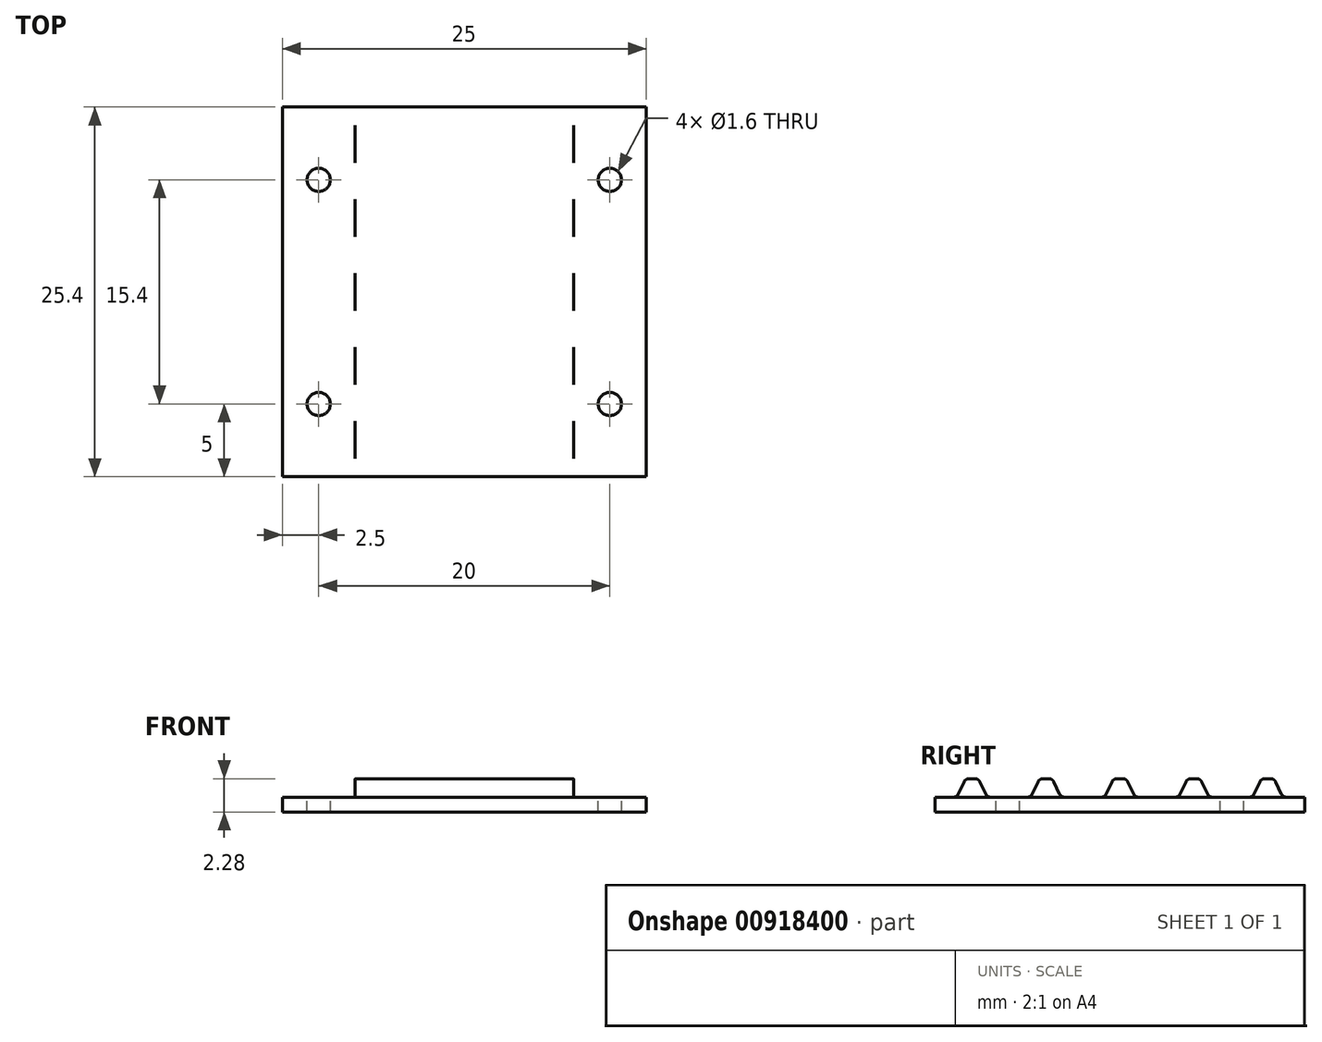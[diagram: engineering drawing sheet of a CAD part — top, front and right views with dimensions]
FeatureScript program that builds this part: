
annotation { "Feature Type Name" : "Feature", "Feature Type Description" : "" }
export const myFeature = defineFeature(function(context is Context, id is Id, definition is map)
    precondition{}
    {
        {
            var Q0;
            Q0=qCreatedBy(makeId("Right.planeOp"),FACE);
            var sketch = newSketch(context, id + "F0", { "sketchPlane" : qUnion([Q0])});
            skArc(sketch, "E0", {"start": v(8.88, -0.13) * mm, "mid": v(9.08, -0.07) * mm, "end": v(9.22, 0.1) * mm});
            skLineSegment(sketch, "E1", {"start": v(9.22, 0.1) * mm, "end": v(9.6, 0.92) * mm});
            skArc(sketch, "E2", {"start": v(9.95, 1.14) * mm, "mid": v(9.75, 1.08) * mm, "end": v(9.6, 0.92) * mm});
            skLineSegment(sketch, "E3", {"start": v(9.95, 1.14) * mm, "end": v(10.37, 1.14) * mm});
            skArc(sketch, "E4", {"start": v(10.7, 0.93) * mm, "mid": v(10.57, 1.08) * mm, "end": v(10.37, 1.14) * mm});
            skLineSegment(sketch, "E5", {"start": v(10.7, 0.93) * mm, "end": v(11.1, 0.1) * mm});
            skArc(sketch, "E6", {"start": v(11.1, 0.1) * mm, "mid": v(11.24, -0.07) * mm, "end": v(11.44, -0.13) * mm});
            skLineSegment(sketch, "E7", {"start": v(11.44, -0.13) * mm, "end": v(12.7, -0.13) * mm});
            skLineSegment(sketch, "E8", {"start": v(12.7, -0.13) * mm, "end": v(12.7, -1.14) * mm});
            skArc(sketch, "E9", {"start": v(3.8, -0.13) * mm, "mid": v(4, -0.07) * mm, "end": v(4.14, 0.1) * mm});
            skLineSegment(sketch, "E10", {"start": v(4.14, 0.1) * mm, "end": v(4.53, 0.92) * mm});
            skArc(sketch, "E11", {"start": v(4.87, 1.14) * mm, "mid": v(4.67, 1.08) * mm, "end": v(4.53, 0.92) * mm});
            skLineSegment(sketch, "E12", {"start": v(4.87, 1.14) * mm, "end": v(5.29, 1.14) * mm});
            skArc(sketch, "E13", {"start": v(5.63, 0.93) * mm, "mid": v(5.49, 1.08) * mm, "end": v(5.29, 1.14) * mm});
            skLineSegment(sketch, "E14", {"start": v(5.63, 0.93) * mm, "end": v(6.02, 0.1) * mm});
            skArc(sketch, "E15", {"start": v(6.02, 0.1) * mm, "mid": v(6.16, -0.07) * mm, "end": v(6.36, -0.13) * mm});
            skLineSegment(sketch, "E16", {"start": v(6.36, -0.13) * mm, "end": v(8.88, -0.13) * mm});
            skArc(sketch, "E17", {"start": v(-1.28, -0.13) * mm, "mid": v(-1.08, -0.07) * mm, "end": v(-0.94, 0.1) * mm});
            skLineSegment(sketch, "E18", {"start": v(-0.94, 0.1) * mm, "end": v(-0.55, 0.92) * mm});
            skArc(sketch, "E19", {"start": v(-0.2, 1.14) * mm, "mid": v(-0.41, 1.08) * mm, "end": v(-0.55, 0.92) * mm});
            skLineSegment(sketch, "E20", {"start": v(-0.2, 1.14) * mm, "end": v(0.2, 1.14) * mm});
            skArc(sketch, "E21", {"start": v(0.55, 0.93) * mm, "mid": v(0.4, 1.08) * mm, "end": v(0.2, 1.14) * mm});
            skLineSegment(sketch, "E22", {"start": v(0.55, 0.93) * mm, "end": v(0.94, 0.1) * mm});
            skArc(sketch, "E23", {"start": v(0.94, 0.1) * mm, "mid": v(1.08, -0.07) * mm, "end": v(1.28, -0.13) * mm});
            skLineSegment(sketch, "E24", {"start": v(1.28, -0.13) * mm, "end": v(3.8, -0.13) * mm});
            skArc(sketch, "E25", {"start": v(-6.36, -0.13) * mm, "mid": v(-6.16, -0.07) * mm, "end": v(-6.02, 0.1) * mm});
            skLineSegment(sketch, "E26", {"start": v(-6.02, 0.1) * mm, "end": v(-5.63, 0.92) * mm});
            skArc(sketch, "E27", {"start": v(-5.29, 1.14) * mm, "mid": v(-5.5, 1.08) * mm, "end": v(-5.63, 0.92) * mm});
            skLineSegment(sketch, "E28", {"start": v(-5.29, 1.14) * mm, "end": v(-4.87, 1.14) * mm});
            skArc(sketch, "E29", {"start": v(-4.53, 0.93) * mm, "mid": v(-4.67, 1.08) * mm, "end": v(-4.87, 1.14) * mm});
            skLineSegment(sketch, "E30", {"start": v(-4.53, 0.93) * mm, "end": v(-4.14, 0.1) * mm});
            skArc(sketch, "E31", {"start": v(-4.14, 0.1) * mm, "mid": v(-4, -0.07) * mm, "end": v(-3.8, -0.13) * mm});
            skLineSegment(sketch, "E32", {"start": v(-3.8, -0.13) * mm, "end": v(-1.28, -0.13) * mm});
            skLineSegment(sketch, "E33", {"start": v(-12.7, -0.13) * mm, "end": v(-11.44, -0.13) * mm});
            skArc(sketch, "E34", {"start": v(-11.44, -0.13) * mm, "mid": v(-11.24, -0.07) * mm, "end": v(-11.1, 0.1) * mm});
            skLineSegment(sketch, "E35", {"start": v(-11.1, 0.1) * mm, "end": v(-10.71, 0.92) * mm});
            skArc(sketch, "E36", {"start": v(-10.37, 1.14) * mm, "mid": v(-10.57, 1.08) * mm, "end": v(-10.71, 0.92) * mm});
            skLineSegment(sketch, "E37", {"start": v(-10.37, 1.14) * mm, "end": v(-9.95, 1.14) * mm});
            skArc(sketch, "E38", {"start": v(-9.61, 0.93) * mm, "mid": v(-9.75, 1.08) * mm, "end": v(-9.95, 1.14) * mm});
            skLineSegment(sketch, "E39", {"start": v(-9.61, 0.93) * mm, "end": v(-9.22, 0.1) * mm});
            skArc(sketch, "E40", {"start": v(-9.22, 0.1) * mm, "mid": v(-9.08, -0.07) * mm, "end": v(-8.88, -0.13) * mm});
            skLineSegment(sketch, "E41", {"start": v(-8.88, -0.13) * mm, "end": v(-6.36, -0.13) * mm});
            skLineSegment(sketch, "E42", {"start": v(12.7, -1.14) * mm, "end": v(-12.7, -1.14) * mm});
            skLineSegment(sketch, "E43", {"start": v(-12.7, -1.14) * mm, "end": v(-12.7, -0.13) * mm});
            skSolve(sketch);
        }
        {
            var Q0;
            Q0=makeQuery(id+"F0.imprint","IMPRINT",FACE,{"disambiguationData":[TD([[makeQuery(id+"F0.imprint","IMPRINT",EDGE,{"derivedFrom":sQuery(id+"F0.wireOp",EDGE,"E0")}),-1.0]])]});
            extrude(context, id + "F1", {"entities" : qUnion([Q0]), "oppositeDirection" : true, "depth" : 7.5 * mm, "offsetDistance" : 25 * mm});
        }
        {
            var Q0;
            Q0=makeQuery(id+"F1.opExtrude","CAP_FACE",FACE,{"disambiguationData":[OSD([sQuery(id+"F0.wireOp",EDGE,"E0"),sQuery(id+"F0.wireOp",EDGE,"E1"),sQuery(id+"F0.wireOp",EDGE,"E2"),sQuery(id+"F0.wireOp",EDGE,"E3"),sQuery(id+"F0.wireOp",EDGE,"E4"),sQuery(id+"F0.wireOp",EDGE,"E5"),sQuery(id+"F0.wireOp",EDGE,"E6"),sQuery(id+"F0.wireOp",EDGE,"E7"),sQuery(id+"F0.wireOp",EDGE,"E8"),sQuery(id+"F0.wireOp",EDGE,"E9"),sQuery(id+"F0.wireOp",EDGE,"E10"),sQuery(id+"F0.wireOp",EDGE,"E11"),sQuery(id+"F0.wireOp",EDGE,"E12"),sQuery(id+"F0.wireOp",EDGE,"E13"),sQuery(id+"F0.wireOp",EDGE,"E14"),sQuery(id+"F0.wireOp",EDGE,"E15"),sQuery(id+"F0.wireOp",EDGE,"E16"),sQuery(id+"F0.wireOp",EDGE,"E17"),sQuery(id+"F0.wireOp",EDGE,"E18"),sQuery(id+"F0.wireOp",EDGE,"E19"),sQuery(id+"F0.wireOp",EDGE,"E20"),sQuery(id+"F0.wireOp",EDGE,"E21"),sQuery(id+"F0.wireOp",EDGE,"E22"),sQuery(id+"F0.wireOp",EDGE,"E23"),sQuery(id+"F0.wireOp",EDGE,"E24"),sQuery(id+"F0.wireOp",EDGE,"E25"),sQuery(id+"F0.wireOp",EDGE,"E26"),sQuery(id+"F0.wireOp",EDGE,"E27"),sQuery(id+"F0.wireOp",EDGE,"E28"),sQuery(id+"F0.wireOp",EDGE,"E29"),sQuery(id+"F0.wireOp",EDGE,"E30"),sQuery(id+"F0.wireOp",EDGE,"E31"),sQuery(id+"F0.wireOp",EDGE,"E32"),sQuery(id+"F0.wireOp",EDGE,"E33"),sQuery(id+"F0.wireOp",EDGE,"E34"),sQuery(id+"F0.wireOp",EDGE,"E35"),sQuery(id+"F0.wireOp",EDGE,"E36"),sQuery(id+"F0.wireOp",EDGE,"E37"),sQuery(id+"F0.wireOp",EDGE,"E38"),sQuery(id+"F0.wireOp",EDGE,"E39"),sQuery(id+"F0.wireOp",EDGE,"E40"),sQuery(id+"F0.wireOp",EDGE,"E41"),sQuery(id+"F0.wireOp",EDGE,"E43"),sQuery(id+"F0.wireOp",EDGE,"e9UeAUZF-xOu5-aih5-fFeQ-uF0AWbEUatni.right"),sQuery(id+"F0.wireOp",EDGE,"qqGL4PSg-W0Be-jaKA-DbFr-9UYhiSR2hx0V")])],"isStart":false});
            var sketch = newSketch(context, id + "F2", { "sketchPlane" : qUnion([Q0])});
            skLineSegment(sketch, "E44", {"start": v(-12.7, -0.13) * mm, "end": v(12.7, -0.13) * mm});
            skSolve(sketch);
        }
        {
            var Q0;
            {var subQ7=makeQuery(id+"F1.opExtrude","CAP_EDGE",EDGE,{"disambiguationData":[OSD([sQuery(id+"F0.wireOp",EDGE,"E43")])],"isStart":false});Q0=makeQuery(id+"F2.imprint","IMPRINT",FACE,{"disambiguationData":[TD([[makeQuery(id+"F2.imprint","IMPRINT",EDGE,{"derivedFrom":subQ7}),1.0]])]});}
            var Q1;
            Q1=qSketchRegion(id+"FQw7OycaFNZsEQX_1",true);
            extrude(context, id + "F3", {"entities" : qUnion([Q0, Q1]), "operationType" : NewBodyOperationType.ADD, "depth" : 5 * mm, "offsetDistance" : 25 * mm});
        }
        {
            var Q0;
            Q0=makeQuery(id+"F1.opExtrude","SWEPT_BODY",BODY,{"disambiguationData":[OSD([sQuery(id+"F0.wireOp",EDGE,"E0"),sQuery(id+"F0.wireOp",EDGE,"E1"),sQuery(id+"F0.wireOp",EDGE,"E2"),sQuery(id+"F0.wireOp",EDGE,"E3"),sQuery(id+"F0.wireOp",EDGE,"E4"),sQuery(id+"F0.wireOp",EDGE,"E5"),sQuery(id+"F0.wireOp",EDGE,"E6"),sQuery(id+"F0.wireOp",EDGE,"E7"),sQuery(id+"F0.wireOp",EDGE,"E8"),sQuery(id+"F0.wireOp",EDGE,"E9"),sQuery(id+"F0.wireOp",EDGE,"E10"),sQuery(id+"F0.wireOp",EDGE,"E11"),sQuery(id+"F0.wireOp",EDGE,"E12"),sQuery(id+"F0.wireOp",EDGE,"E13"),sQuery(id+"F0.wireOp",EDGE,"E14"),sQuery(id+"F0.wireOp",EDGE,"E15"),sQuery(id+"F0.wireOp",EDGE,"E16"),sQuery(id+"F0.wireOp",EDGE,"E17"),sQuery(id+"F0.wireOp",EDGE,"E18"),sQuery(id+"F0.wireOp",EDGE,"E19"),sQuery(id+"F0.wireOp",EDGE,"E20"),sQuery(id+"F0.wireOp",EDGE,"E21"),sQuery(id+"F0.wireOp",EDGE,"E22"),sQuery(id+"F0.wireOp",EDGE,"E23"),sQuery(id+"F0.wireOp",EDGE,"E24"),sQuery(id+"F0.wireOp",EDGE,"E25"),sQuery(id+"F0.wireOp",EDGE,"E26"),sQuery(id+"F0.wireOp",EDGE,"E27"),sQuery(id+"F0.wireOp",EDGE,"E28"),sQuery(id+"F0.wireOp",EDGE,"E29"),sQuery(id+"F0.wireOp",EDGE,"E30"),sQuery(id+"F0.wireOp",EDGE,"E31"),sQuery(id+"F0.wireOp",EDGE,"E32"),sQuery(id+"F0.wireOp",EDGE,"E33"),sQuery(id+"F0.wireOp",EDGE,"E34"),sQuery(id+"F0.wireOp",EDGE,"E35"),sQuery(id+"F0.wireOp",EDGE,"E36"),sQuery(id+"F0.wireOp",EDGE,"E37"),sQuery(id+"F0.wireOp",EDGE,"E38"),sQuery(id+"F0.wireOp",EDGE,"E39"),sQuery(id+"F0.wireOp",EDGE,"E40"),sQuery(id+"F0.wireOp",EDGE,"E41"),sQuery(id+"F0.wireOp",EDGE,"E43"),sQuery(id+"F0.wireOp",EDGE,"e9UeAUZF-xOu5-aih5-fFeQ-uF0AWbEUatni.right"),sQuery(id+"F0.wireOp",EDGE,"qqGL4PSg-W0Be-jaKA-DbFr-9UYhiSR2hx0V")])]});
            var Q1;
            Q1=qCreatedBy(makeId("Right.planeOp"),FACE);
            mirror(context, id + "F4", {"operationType" : NewBodyOperationType.ADD, "entities" : qUnion([Q0]), "mirrorPlane" : qUnion([Q1])});
        }
        {
            var Q0;
            {var subQ0=makeQuery(id+"F3.boolean.opBoolean","MERGE",FACE,{"derivedFrom":[makeQuery(id+"F1.opExtrude","SWEPT_FACE",FACE,{"disambiguationData":[OSD([sQuery(id+"F0.wireOp",EDGE,"E7")])]}),makeQuery(id+"F1.opExtrude","SWEPT_FACE",FACE,{"disambiguationData":[OSD([sQuery(id+"F0.wireOp",EDGE,"E16")])]}),makeQuery(id+"F1.opExtrude","SWEPT_FACE",FACE,{"disambiguationData":[OSD([sQuery(id+"F0.wireOp",EDGE,"E24")])]}),makeQuery(id+"F1.opExtrude","SWEPT_FACE",FACE,{"disambiguationData":[OSD([sQuery(id+"F0.wireOp",EDGE,"E32")])]}),makeQuery(id+"F1.opExtrude","SWEPT_FACE",FACE,{"disambiguationData":[OSD([sQuery(id+"F0.wireOp",EDGE,"E33")])]}),makeQuery(id+"F1.opExtrude","SWEPT_FACE",FACE,{"disambiguationData":[OSD([sQuery(id+"F0.wireOp",EDGE,"E41")])]}),makeQuery(id+"F3.opExtrude","SWEPT_FACE",FACE,{"disambiguationData":[OSD([sQuery(id+"F2.wireOp",EDGE,"E44")])]})]});Q0=makeQuery(id+"F4.boolean.opBoolean","MERGE",FACE,{"derivedFrom":[subQ0,makeQuery(id+"F4.opPattern","COPY",FACE,{"derivedFrom":subQ0,"instanceName":"1"})]});}
            var sketch = newSketch(context, id + "F5", { "sketchPlane" : qUnion([Q0])});
            skCircle(sketch, "E45", {"center": v(10, 7.7) * mm, "radius": 0.8 * mm});
            skCircle(sketch, "E46", {"center": v(10, -7.7) * mm, "radius": 0.8 * mm});
            skCircle(sketch, "E47.MirrorC", {"center": v(-10, 7.7) * mm, "radius": 0.8 * mm});
            skCircle(sketch, "E48.MirrorC", {"center": v(-10, -7.7) * mm, "radius": 0.8 * mm});
            skSolve(sketch);
        }
        {
            var Q0;
            Q0=qSketchRegion(id+"F5",true);
            extrude(context, id + "F6", {"entities" : qUnion([Q0]), "operationType" : NewBodyOperationType.REMOVE, "oppositeDirection" : true, "depth" : 45 * mm, "offsetDistance" : 25 * mm});
        }
    });
